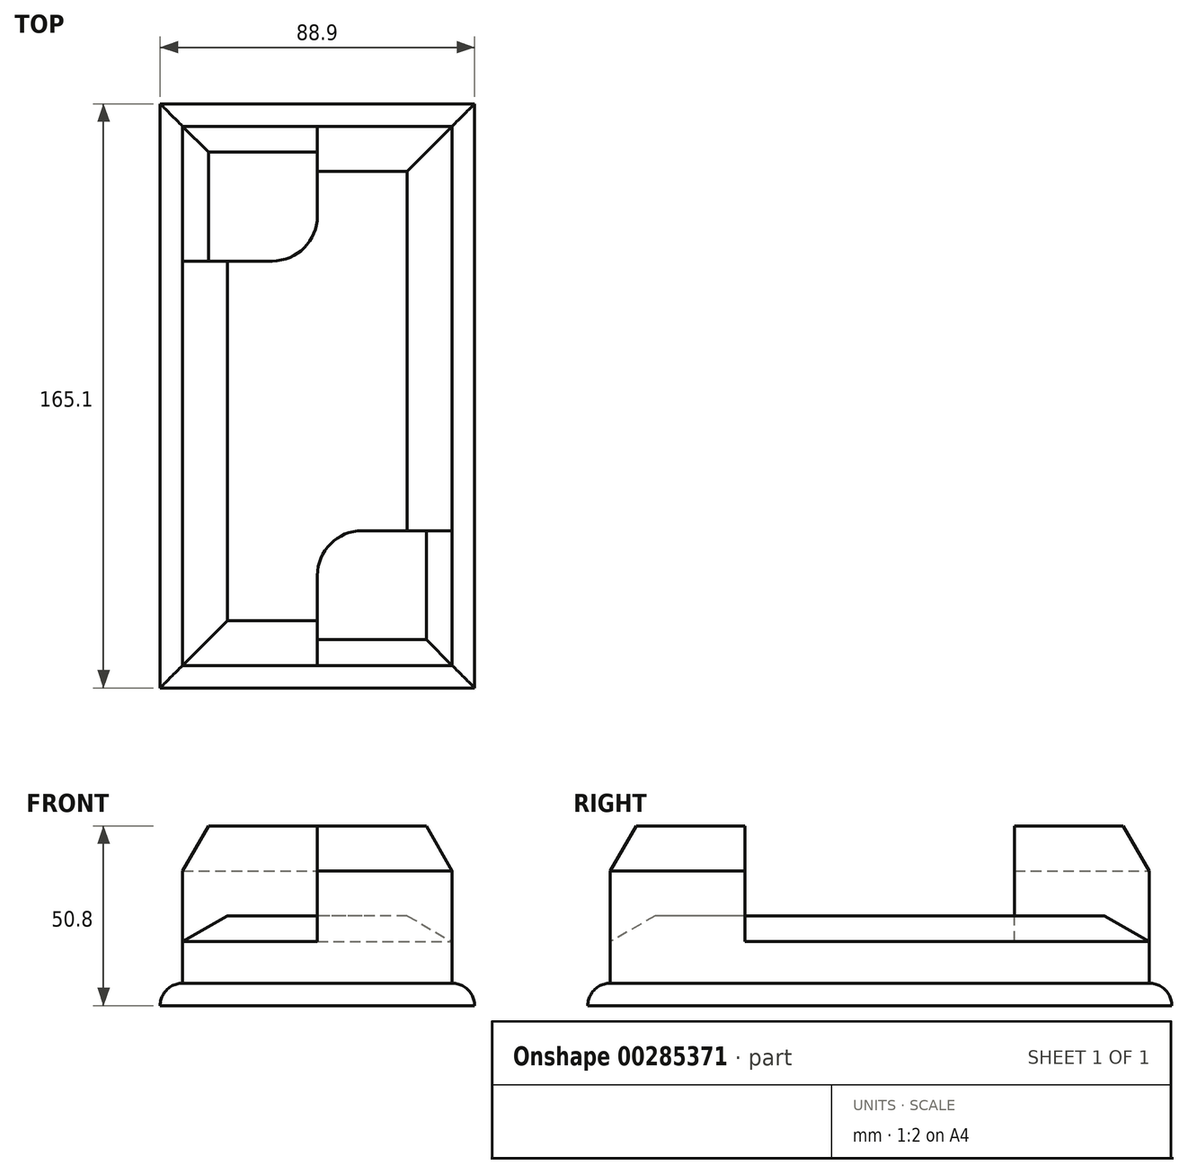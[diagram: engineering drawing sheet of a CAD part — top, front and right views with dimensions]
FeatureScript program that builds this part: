
annotation { "Feature Type Name" : "Feature", "Feature Type Description" : "" }
export const myFeature = defineFeature(function(context is Context, id is Id, definition is map)
    precondition{}
    {
        {
            var Q0;
            Q0=qCreatedBy(makeId("Top.planeOp"),FACE);
            var sketch = newSketch(context, id + "F0", { "sketchPlane" : qUnion([Q0])});
            skLineSegment(sketch, "E0.bottom", {"start": v(6.35, -6.35) * mm, "end": v(82.55, -6.35) * mm});
            skLineSegment(sketch, "E0.top", {"start": v(6.35, -158.75) * mm, "end": v(82.55, -158.75) * mm});
            skLineSegment(sketch, "E0.left", {"start": v(6.35, -6.35) * mm, "end": v(6.35, -158.75) * mm});
            skLineSegment(sketch, "E0.right", {"start": v(82.55, -6.35) * mm, "end": v(82.55, -158.75) * mm});
            skLineSegment(sketch, "E1", {"start": v(6.35, -44.45) * mm, "end": v(31.75, -44.45) * mm});
            skLineSegment(sketch, "E2", {"start": v(44.45, -31.75) * mm, "end": v(44.45, -6.35) * mm});
            skLineSegment(sketch, "E3", {"start": v(82.55, -120.65) * mm, "end": v(57.15, -120.65) * mm});
            skLineSegment(sketch, "E4", {"start": v(44.45, -133.35) * mm, "end": v(44.45, -158.75) * mm});
            skPoint(sketch, "E5.visualSharp", {"position": v(44.45, -44.45) * mm});
            skArc(sketch, "E5.filletArc", {"start": v(31.75, -44.45) * mm, "mid": v(40.73, -40.73) * mm, "end": v(44.45, -31.75) * mm});
            skPoint(sketch, "E6.visualSharp", {"position": v(44.45, -120.65) * mm});
            skArc(sketch, "E6.filletArc", {"start": v(57.15, -120.65) * mm, "mid": v(48.17, -124.37) * mm, "end": v(44.45, -133.35) * mm});
            skLineSegment(sketch, "E7.0", {"start": v(0, 0) * mm, "end": v(0, -165.1) * mm});
            skLineSegment(sketch, "E7.1", {"start": v(0, 0) * mm, "end": v(88.9, 0) * mm});
            skLineSegment(sketch, "E7.2", {"start": v(88.9, 0) * mm, "end": v(88.9, -165.1) * mm});
            skLineSegment(sketch, "E7.3", {"start": v(0, -165.1) * mm, "end": v(88.9, -165.1) * mm});
            skSolve(sketch);
        }
        {
            var Q0;
            Q0=makeQuery(id+"F0.imprint","IMPRINT",FACE,{"disambiguationData":[TD([[makeQuery(id+"F0.imprint","IMPRINT",EDGE,{"derivedFrom":sQuery(id+"F0.wireOp",EDGE,"E7.0")}),1.0]])]});
            extrude(context, id + "F1", {"entities" : qUnion([Q0]), "depth" : 6.35 * mm});
        }
        {
            var Q0;
            {var subQ3=sQuery(id+"F0.wireOp",EDGE,"E1");Q0=makeQuery(id+"F0.imprint","IMPRINT",FACE,{"disambiguationData":[TD([[makeQuery(id+"F0.imprint","IMPRINT",EDGE,{"derivedFrom":subQ3}),-1.0]])]});}
            extrude(context, id + "F2", {"entities" : qUnion([Q0]), "operationType" : NewBodyOperationType.ADD, "depth" : 25.4 * mm});
        }
        {
            var Q0;
            {var subQ0=sQuery(id+"F0.wireOp",EDGE,"E1");Q0=makeQuery(id+"F0.imprint","IMPRINT",FACE,{"disambiguationData":[TD([[makeQuery(id+"F0.imprint","IMPRINT",EDGE,{"derivedFrom":subQ0}),1.0]])]});}
            var Q1;
            {var subQ1=sQuery(id+"F0.wireOp",EDGE,"E3");Q1=makeQuery(id+"F0.imprint","IMPRINT",FACE,{"disambiguationData":[TD([[makeQuery(id+"F0.imprint","IMPRINT",EDGE,{"derivedFrom":subQ1}),1.0]])]});}
            extrude(context, id + "F3", {"entities" : qUnion([Q0, Q1]), "operationType" : NewBodyOperationType.ADD, "depth" : 50.8 * mm});
        }
        {
            var Q0;
            Q0=makeQuery(id+"F1.opExtrude","CAP_EDGE",EDGE,{"disambiguationData":[OSD([sQuery(id+"F0.wireOp",EDGE,"E7.3")])],"isStart":false});
            var Q1;
            Q1=makeQuery(id+"F1.opExtrude","CAP_EDGE",EDGE,{"disambiguationData":[OSD([sQuery(id+"F0.wireOp",EDGE,"E7.2")])],"isStart":false});
            var Q2;
            Q2=makeQuery(id+"F1.opExtrude","CAP_EDGE",EDGE,{"disambiguationData":[OSD([sQuery(id+"F0.wireOp",EDGE,"E7.0")])],"isStart":false});
            var Q3;
            Q3=makeQuery(id+"F1.opExtrude","CAP_EDGE",EDGE,{"disambiguationData":[OSD([sQuery(id+"F0.wireOp",EDGE,"E7.1")])],"isStart":false});
            fillet(context, id + "F4", {"entities" : qUnion([Q0, Q1, Q2, Q3]), "radius" : 6.35 * mm, "tangentPropagation" : true, "allowEdgeOverflow" : false});
        }
        {
            var Q0;
            Q0=makeQuery(id+"F2.opExtrude","CAP_EDGE",EDGE,{"disambiguationData":[OSD([sQuery(id+"F0.wireOp",EDGE,"E0.top")])],"isStart":false});
            var Q1;
            Q1=makeQuery(id+"F2.opExtrude","CAP_EDGE",EDGE,{"disambiguationData":[OSD([sQuery(id+"F0.wireOp",EDGE,"E0.bottom")])],"isStart":false});
            var Q2;
            Q2=makeQuery(id+"F2.opExtrude","CAP_EDGE",EDGE,{"disambiguationData":[OSD([sQuery(id+"F0.wireOp",EDGE,"E0.right")])],"isStart":false});
            var Q3;
            Q3=makeQuery(id+"F2.opExtrude","CAP_EDGE",EDGE,{"disambiguationData":[OSD([sQuery(id+"F0.wireOp",EDGE,"E0.left")])],"isStart":false});
            chamfer(context, id + "F5", {"entities" : qUnion([Q0, Q1, Q2, Q3]), "chamferType" : ChamferType.OFFSET_ANGLE, "width" : 12.7 * mm, "oppositeDirection" : false, "angle" : 30 * degree, "tangentPropagation" : true});
        }
        {
            var Q0;
            Q0=makeQuery(id+"F3.opExtrude","CAP_EDGE",EDGE,{"disambiguationData":[OSD([sQuery(id+"F0.wireOp",EDGE,"E0.left")])],"isStart":false});
            var Q1;
            Q1=makeQuery(id+"F3.opExtrude","CAP_EDGE",EDGE,{"disambiguationData":[OSD([sQuery(id+"F0.wireOp",EDGE,"E0.bottom")])],"isStart":false});
            chamfer(context, id + "F6", {"entities" : qUnion([Q0, Q1]), "chamferType" : ChamferType.OFFSET_ANGLE, "width" : 12.7 * mm, "oppositeDirection" : true, "angle" : 30 * degree, "tangentPropagation" : true});
        }
        {
            var Q0;
            Q0=makeQuery(id+"F3.opExtrude","CAP_EDGE",EDGE,{"disambiguationData":[OSD([sQuery(id+"F0.wireOp",EDGE,"E0.right")])],"isStart":false});
            var Q1;
            Q1=makeQuery(id+"F3.opExtrude","CAP_EDGE",EDGE,{"disambiguationData":[OSD([sQuery(id+"F0.wireOp",EDGE,"E0.top")])],"isStart":false});
            chamfer(context, id + "F7", {"entities" : qUnion([Q0, Q1]), "chamferType" : ChamferType.OFFSET_ANGLE, "width" : 12.7 * mm, "oppositeDirection" : false, "angle" : 30 * degree, "tangentPropagation" : true});
        }
    });
